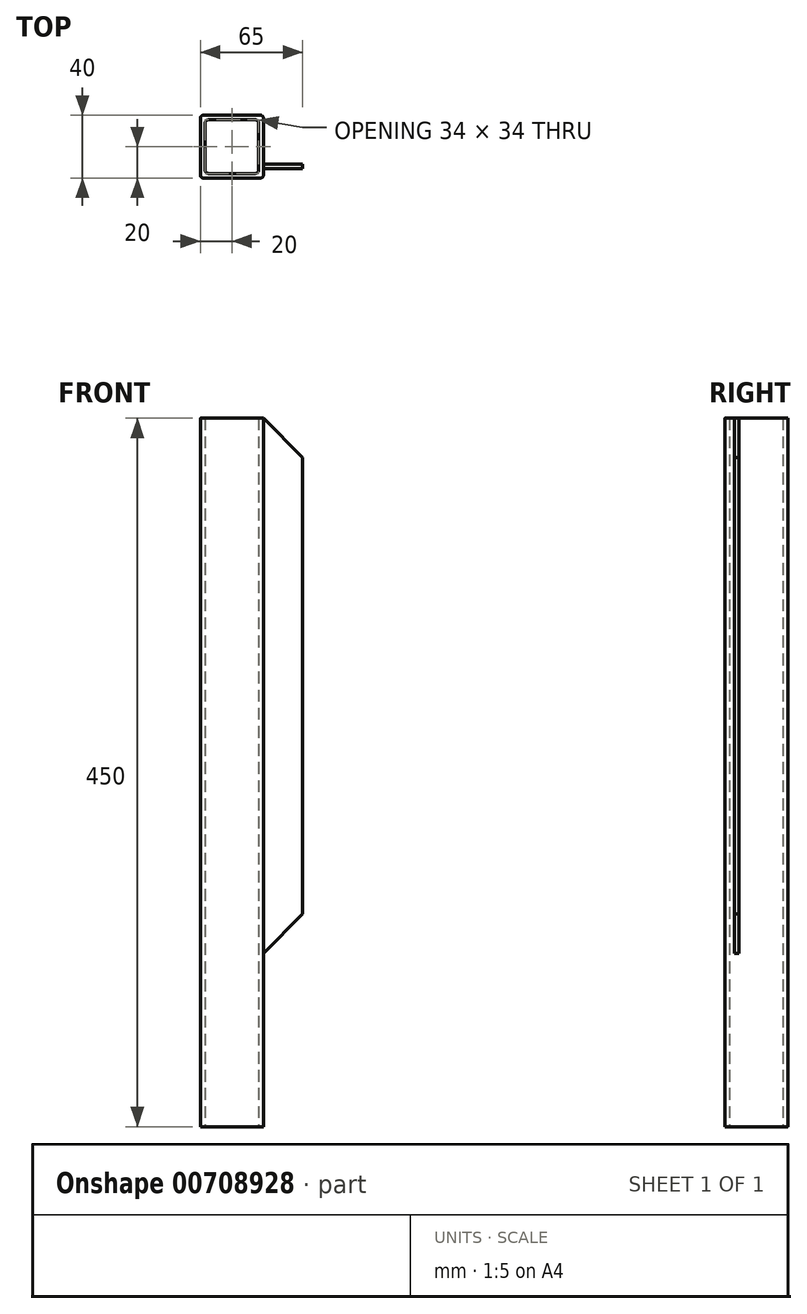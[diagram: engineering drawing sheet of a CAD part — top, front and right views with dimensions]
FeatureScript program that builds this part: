
annotation { "Feature Type Name" : "Feature", "Feature Type Description" : "" }
export const myFeature = defineFeature(function(context is Context, id is Id, definition is map)
    precondition{}
    {
        {
            var Q0;
            Q0=qCreatedBy(makeId("Top.planeOp"),FACE);
            var sketch = newSketch(context, id + "F0", { "sketchPlane" : qUnion([Q0])});
            skLineSegment(sketch, "E0.bottom", {"start": v(15, 17) * mm, "end": v(-15, 17) * mm});
            skLineSegment(sketch, "E0.top", {"start": v(15, -17) * mm, "end": v(-15, -17) * mm});
            skLineSegment(sketch, "E0.left", {"start": v(17, 15) * mm, "end": v(17, -15) * mm});
            skLineSegment(sketch, "E0.right", {"start": v(-17, 15) * mm, "end": v(-17, -15) * mm});
            skPoint(sketch, "E0.middle", {"position": v(0, 0) * mm});
            skLineSegment(sketch, "E1.0", {"start": v(18, 20) * mm, "end": v(-18, 20) * mm});
            skLineSegment(sketch, "E1.1", {"start": v(20, 18) * mm, "end": v(20, -18) * mm});
            skLineSegment(sketch, "E1.2", {"start": v(18, -20) * mm, "end": v(-18, -20) * mm});
            skLineSegment(sketch, "E1.3", {"start": v(-20, 18) * mm, "end": v(-20, -18) * mm});
            skPoint(sketch, "E2.visualSharp", {"position": v(-20, 20) * mm});
            skArc(sketch, "E2.filletArc", {"start": v(-18, 20) * mm, "mid": v(-19.41, 19.41) * mm, "end": v(-20, 18) * mm});
            skPoint(sketch, "E3.visualSharp", {"position": v(-17, 17) * mm});
            skArc(sketch, "E3.filletArc", {"start": v(-15, 17) * mm, "mid": v(-16.41, 16.41) * mm, "end": v(-17, 15) * mm});
            skPoint(sketch, "E4.visualSharp", {"position": v(17, 17) * mm});
            skArc(sketch, "E4.filletArc", {"start": v(17, 15) * mm, "mid": v(16.41, 16.41) * mm, "end": v(15, 17) * mm});
            skPoint(sketch, "E5.visualSharp", {"position": v(20, 20) * mm});
            skArc(sketch, "E5.filletArc", {"start": v(20, 18) * mm, "mid": v(19.41, 19.41) * mm, "end": v(18, 20) * mm});
            skPoint(sketch, "E6.visualSharp", {"position": v(20, -20) * mm});
            skArc(sketch, "E6.filletArc", {"start": v(18, -20) * mm, "mid": v(19.41, -19.41) * mm, "end": v(20, -18) * mm});
            skPoint(sketch, "E7.visualSharp", {"position": v(17, -17) * mm});
            skArc(sketch, "E7.filletArc", {"start": v(15, -17) * mm, "mid": v(16.41, -16.41) * mm, "end": v(17, -15) * mm});
            skPoint(sketch, "E8.visualSharp", {"position": v(-17, -17) * mm});
            skArc(sketch, "E8.filletArc", {"start": v(-17, -15) * mm, "mid": v(-16.41, -16.41) * mm, "end": v(-15, -17) * mm});
            skPoint(sketch, "E9.visualSharp", {"position": v(-20, -20) * mm});
            skArc(sketch, "E9.filletArc", {"start": v(-20, -18) * mm, "mid": v(-19.41, -19.41) * mm, "end": v(-18, -20) * mm});
            skSolve(sketch);
        }
        {
            var Q0;
            Q0=makeQuery(id+"F0.imprint","IMPRINT",FACE,{"disambiguationData":[TD([[makeQuery(id+"F0.imprint","IMPRINT",EDGE,{"derivedFrom":sQuery(id+"F0.wireOp",EDGE,"E0.bottom")}),-1.0]])]});
            var Q1;
            Q1=sQuery(id+"F0.wireOp",EDGE,"E1.0");
            extrude(context, id + "F1", {"entities" : qUnion([Q0]), "surfaceEntities" : qUnion([Q1]), "endBound" : BoundingType.SYMMETRIC, "depth" : 450 * mm, "offsetDistance" : 25 * mm});
        }
        {
            var Q0;
            Q0=makeQuery(id+"F1.opExtrude","SWEPT_FACE",FACE,{"disambiguationData":[OSD([sQuery(id+"F0.wireOp",EDGE,"E1.1")])]});
            var sketch = newSketch(context, id + "F2", { "sketchPlane" : qUnion([Q0])});
            skLineSegment(sketch, "E10.bottom", {"start": v(-14, -115) * mm, "end": v(-11, -115) * mm});
            skLineSegment(sketch, "E10.top", {"start": v(-14, 225) * mm, "end": v(-11, 225) * mm});
            skLineSegment(sketch, "E10.left", {"start": v(-14, -115) * mm, "end": v(-14, 225) * mm});
            skLineSegment(sketch, "E10.right", {"start": v(-11, -115) * mm, "end": v(-11, 225) * mm});
            skLineSegment(sketch, "E11", {"start": v(0, 225) * mm, "end": v(0, -225) * mm, "construction": true});
            skSolve(sketch);
        }
        {
            var Q0;
            Q0=makeQuery(id+"F2.imprint","IMPRINT",FACE,{"disambiguationData":[TD([[makeQuery(id+"F2.imprint","IMPRINT",EDGE,{"derivedFrom":sQuery(id+"F2.wireOp",EDGE,"E10.bottom")}),1.0]])]});
            extrude(context, id + "F3", {"entities" : qUnion([Q0]), "operationType" : NewBodyOperationType.ADD, "depth" : 25 * mm, "offsetDistance" : 25 * mm});
        }
        {
            var Q0;
            Q0=makeQuery(id+"F3.opExtrude","SWEPT_FACE",FACE,{"disambiguationData":[OSD([sQuery(id+"F2.wireOp",EDGE,"E10.left")])]});
            var sketch = newSketch(context, id + "F4", { "sketchPlane" : qUnion([Q0])});
            skLineSegment(sketch, "E12", {"start": v(20, 225) * mm, "end": v(45, 200) * mm});
            skLineSegment(sketch, "E13", {"start": v(45, 200) * mm, "end": v(20, 225) * mm});
            skLineSegment(sketch, "E14", {"start": v(45, 200) * mm, "end": v(45, 225) * mm});
            skLineSegment(sketch, "E15", {"start": v(45, 225) * mm, "end": v(20, 225) * mm});
            skLineSegment(sketch, "E16", {"start": v(45, -90) * mm, "end": v(20, -115) * mm});
            skLineSegment(sketch, "E17", {"start": v(20, -115) * mm, "end": v(45, -115) * mm});
            skLineSegment(sketch, "E18", {"start": v(45, -115) * mm, "end": v(45, -90) * mm});
            skSolve(sketch);
        }
        {
            var Q0;
            Q0 = qSketchRegion(id + "F4", true);
            extrude(context, id + "F5", {"entities" : qUnion([Q0]), "operationType" : NewBodyOperationType.REMOVE, "endBound" : BoundingType.THROUGH_ALL, "oppositeDirection" : true, "depth" : 25 * mm, "offsetDistance" : 25 * mm});
        }
    });
